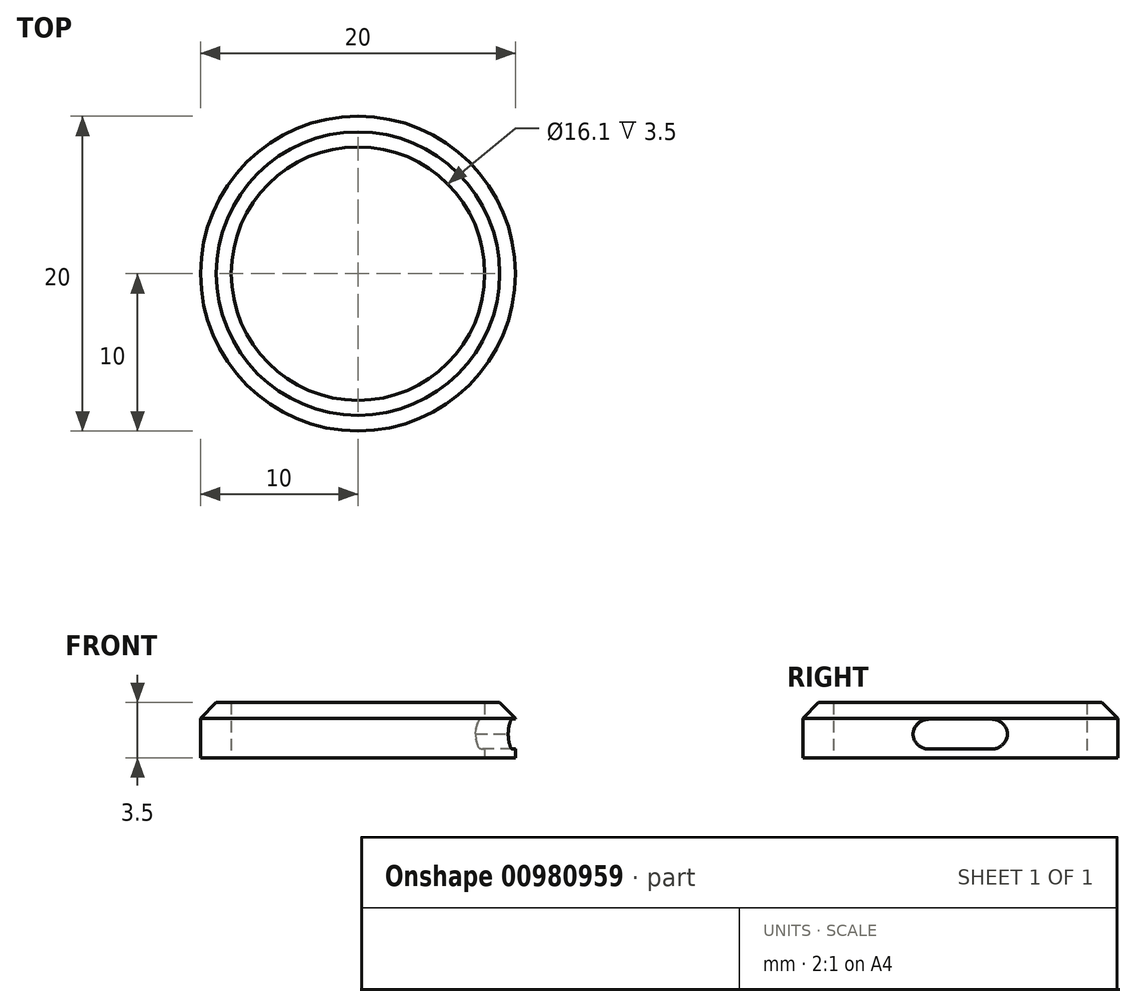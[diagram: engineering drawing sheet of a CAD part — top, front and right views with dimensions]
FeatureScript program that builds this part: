
annotation { "Feature Type Name" : "Feature", "Feature Type Description" : "" }
export const myFeature = defineFeature(function(context is Context, id is Id, definition is map)
    precondition{}
    {
        {
            var Q0;
            Q0=qCreatedBy(makeId("Top.planeOp"),FACE);
            var sketch = newSketch(context, id + "F0", { "sketchPlane" : qUnion([Q0])});
            skCircle(sketch, "E0", {"center": v(0, 0) * mm, "radius": 10 * mm});
            skCircle(sketch, "E1", {"center": v(0, 0) * mm, "radius": 8.05 * mm});
            skSolve(sketch);
        }
        {
            var Q0;
            Q0=makeQuery(id+"F0.imprint","IMPRINT",FACE,{"disambiguationData":[TD([[makeQuery(id+"F0.imprint","IMPRINT",EDGE,{"derivedFrom":sQuery(id+"F0.wireOp",EDGE,"E0")}),1.0]])]});
            extrude(context, id + "F1", {"entities" : qUnion([Q0]), "depth" : 3.5 * mm, "offsetDistance" : 25 * mm});
        }
        {
            var Q0;
            Q0=qCreatedBy(makeId("Right.planeOp"),FACE);
            var sketch = newSketch(context, id + "F2", { "sketchPlane" : qUnion([Q0])});
            skLineSegment(sketch, "E2", {"start": v(0, 0) * mm, "end": v(0, 1.5) * mm});
            skLineSegment(sketch, "E3.bottom", {"start": v(3, 2.45) * mm, "end": v(-3, 2.45) * mm});
            skLineSegment(sketch, "E3.top", {"start": v(3, 0.55) * mm, "end": v(-3, 0.55) * mm});
            skLineSegment(sketch, "E3.left", {"start": v(3, 2.45) * mm, "end": v(3, 0.55) * mm});
            skLineSegment(sketch, "E3.right", {"start": v(-3, 2.45) * mm, "end": v(-3, 0.55) * mm});
            skPoint(sketch, "E3.middle", {"position": v(0, 1.5) * mm});
            skSolve(sketch);
        }
        {
            var Q0;
            Q0=makeQuery(id+"F2.imprint","IMPRINT",FACE,{"disambiguationData":[TD([[makeQuery(id+"F2.imprint","IMPRINT",EDGE,{"derivedFrom":sQuery(id+"F2.wireOp",EDGE,"E3.bottom")}),1.0]])]});
            extrude(context, id + "F3", {"entities" : qUnion([Q0]), "operationType" : NewBodyOperationType.REMOVE, "depth" : 16.9 * mm, "offsetDistance" : 25 * mm});
        }
        {
            var Q0;
            Q0=makeQuery(id+"F3.boolean.opBoolean","COPY",EDGE,{"derivedFrom":makeQuery(id+"F3.opExtrude","SWEPT_EDGE",EDGE,{"disambiguationData":[OSD([sQuery(id+"F2.wireOp",EDGE,"E3.bottom"),sQuery(id+"F2.wireOp",EDGE,"E3.left")])]})});
            var Q1;
            Q1=makeQuery(id+"F3.boolean.opBoolean","COPY",EDGE,{"derivedFrom":makeQuery(id+"F3.opExtrude","SWEPT_EDGE",EDGE,{"disambiguationData":[OSD([sQuery(id+"F2.wireOp",EDGE,"E3.top"),sQuery(id+"F2.wireOp",EDGE,"E3.left")])]})});
            var Q2;
            Q2=makeQuery(id+"F3.boolean.opBoolean","COPY",EDGE,{"derivedFrom":makeQuery(id+"F3.opExtrude","SWEPT_EDGE",EDGE,{"disambiguationData":[OSD([sQuery(id+"F2.wireOp",EDGE,"E3.bottom"),sQuery(id+"F2.wireOp",EDGE,"E3.right")])]})});
            var Q3;
            Q3=makeQuery(id+"F3.boolean.opBoolean","COPY",EDGE,{"derivedFrom":makeQuery(id+"F3.opExtrude","SWEPT_EDGE",EDGE,{"disambiguationData":[OSD([sQuery(id+"F2.wireOp",EDGE,"E3.top"),sQuery(id+"F2.wireOp",EDGE,"E3.right")])]})});
            fillet(context, id + "F4", {"entities" : qUnion([Q0, Q1, Q2, Q3]), "radius" : 1 * mm, "tangentPropagation" : true, "allowEdgeOverflow" : false});
        }
        {
            var Q0;
            Q0=makeQuery(id+"F1.opExtrude","CAP_EDGE",EDGE,{"disambiguationData":[OSD([sQuery(id+"F0.wireOp",EDGE,"E0")])],"isStart":false});
            chamfer(context, id + "F5", {"entities" : qUnion([Q0]), "width" : 1 * mm, "tangentPropagation" : true});
        }
    });
